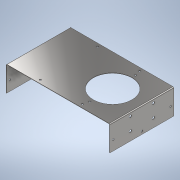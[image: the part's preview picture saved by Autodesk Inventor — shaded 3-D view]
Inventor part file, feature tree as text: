
AUTODESK INVENTOR PART (.ipt)
format: ipt  version: 2020 (Build 240168000, 168)  size: 198,144 bytes
history: native  units: mm
features: sheet_metal_op x7, sketch x7, hole x3, other x3, extrude x1
ambient origin geometry x8: Origin, YZ Plane, XZ Plane, XY Plane, X Axis, Y Axis, Z Axis, Center Point
bodies: Solid1 (feature_tree)
feature tree (21):
  sheet_metal_op  "Face1"
  sheet_metal_op  "Flange1"
  sheet_metal_op  "Flange2"
  extrude  "Extrusion1"  Depth=155.0mm
  hole  "Hole1"  [1 undecoded]
  hole  "Hole2"  [1 undecoded]
  hole  "Hole3"  [1 undecoded]
  sketch  "Sketch1"  dims[d0=252.0mm d1=155.0mm]
  other  "Plate1"
  sketch  "Sketch2"  dims[d2=1.0mm d3=1.0mm]
  other  "Plate2"
  sheet_metal_op  "Bend1"
  sheet_metal_op  "Corner1"
  sketch  "Sketch3"  dims[d4=0.5mm d5=2.0mm]
  other  "Plate3"
  sheet_metal_op  "Bend2"
  sheet_metal_op  "Corner2"
  sketch  "Sketch4"  dims[d6=1.0mm d7=61.0mm d8=90.0deg d9=1.0mm]
  sketch  "Sketch5"  dims[d10=4.0mm]
  sketch  "Sketch6"  dims[d11=1.0mm]
  sketch  "Sketch7"  dims[d12=1.0mm d13=1.0mm d14=0.5mm d15=2.0mm d16=1.0mm d17=61.0mm d18=90.0deg d19=1.0mm d20=4.0mm d21=1.0mm d22=1.0mm d23=77.5mm d24=71.0mm d25=94.0mm d26=55.5mm d27=55.5mm d28=4.5mm d29=4.5mm d30=0.0mm d31=0.0mm d32=75.0mm d33=75.0mm d34=8.0mm d35=8.0mm d36=4.5mm d37=12.0mm d38=4.0mm d39=2.0mm d40=90.0deg d41=1.0mm d42=20.594885mm d43=77.5mm d44=7.0mm d45=8.0mm d46=8.0mm d47=24.0mm d48=24.0mm d49=4.5mm d50=12.0mm d51=4.0mm d52=2.0mm d53=90.0deg d54=1.0mm d55=20.594885mm d57=35.0mm d58=45.0mm d59=70.0mm d60=7.0mm d61=7.0mm d62=7.0mm d63=7.0mm d64=6.0mm d65=12.0mm d66=4.0mm d67=2.0mm d68=90.0deg d69=1.0mm d70=20.594885mm]
note: 3 required parameter values undecoded (feature->parameter linkage not recoverable at this tier; creation-order binding heuristic only, values carry confidence <= 0.55)
